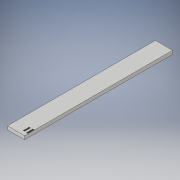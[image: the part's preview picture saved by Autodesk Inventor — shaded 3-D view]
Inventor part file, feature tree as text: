
AUTODESK INVENTOR PART (.ipt)
format: ipt  version: 2019.4 (Build 234330000, 330)  size: 198,144 bytes
history: native  units: in
note: dims shown in document units (in); Inventor stores cm internally (conversion verified against a paired STEP export)
features: extrude x2, sketch x2
ambient origin geometry x8: Origin, YZ Plane, XZ Plane, XY Plane, X Axis, Y Axis, Z Axis, Center Point
bodies: Solid1 (feature_tree)
feature tree (4):
  extrude  "Extrusion1"  Depth=0.1969in
  extrude  "Extrusion2"  Depth=0.0039in
  sketch  "Sketch1"  dims[d0=1.6929in d1=0.1969in]
  sketch  "Sketch2"  dims[d2=0.0394in d3=0.0in d4=0.0039in d5=0.0157in d6=0.0039in d7=0.0394in d8=3.937in d10=0.0079in d11=0.3937in d13=0.3937in d15=0.0433in d16=0.0394in d17=3.5433in d19=0.0079in d20=0.3937in d22=0.3937in d24=0.0012in d25=0.0in]
